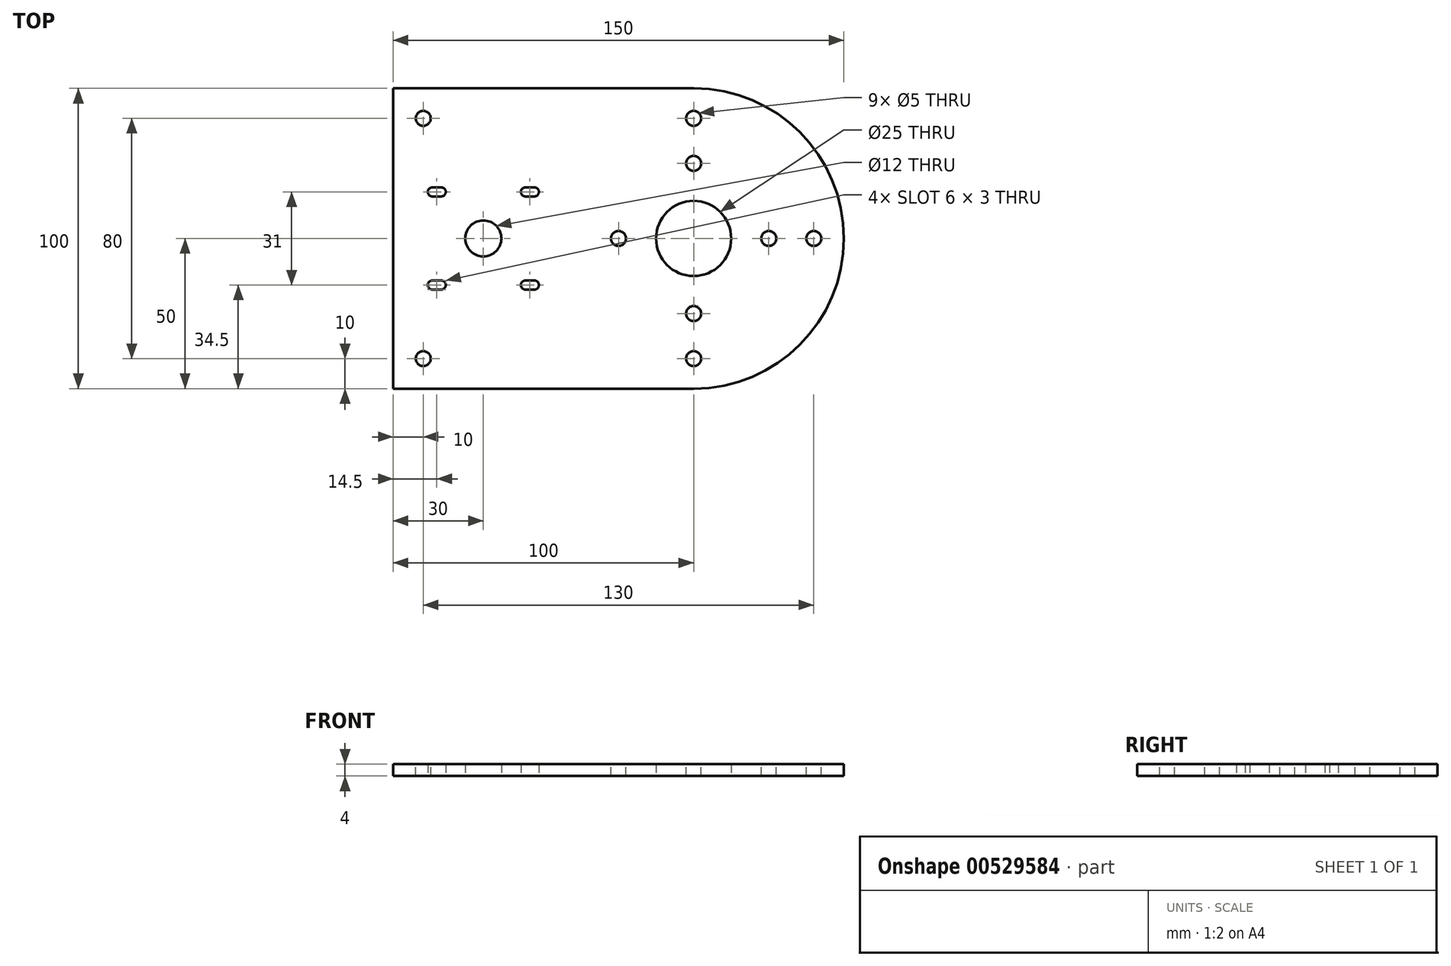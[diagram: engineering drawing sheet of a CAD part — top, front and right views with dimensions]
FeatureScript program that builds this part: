
annotation { "Feature Type Name" : "Feature", "Feature Type Description" : "" }
export const myFeature = defineFeature(function(context is Context, id is Id, definition is map)
    precondition{}
    {
        {
            var Q0;
            Q0=qCreatedBy(makeId("Top.planeOp"),FACE);
            var sketch = newSketch(context, id + "F0", { "sketchPlane" : qUnion([Q0])});
            skArc(sketch, "E0", {"start": v(0, -50) * mm, "mid": v(50, 0) * mm, "end": v(0, 50) * mm});
            skLineSegment(sketch, "E1", {"start": v(0, 50) * mm, "end": v(-100, 50) * mm});
            skLineSegment(sketch, "E2", {"start": v(-100, 50) * mm, "end": v(-100, -50) * mm});
            skLineSegment(sketch, "E3", {"start": v(-100, -50) * mm, "end": v(0, -50) * mm});
            skCircle(sketch, "E4", {"center": v(0, 0) * mm, "radius": 12.5 * mm});
            skPoint(sketch, "E5", {"position": v(-70, 0) * mm});
            skCircle(sketch, "E6", {"center": v(-70, 0) * mm, "radius": 6 * mm});
            skLineSegment(sketch, "E7.bottom", {"start": v(-53, -14) * mm, "end": v(-56, -14) * mm});
            skLineSegment(sketch, "E7.top", {"start": v(-53, -17) * mm, "end": v(-56, -17) * mm});
            skLineSegment(sketch, "E7.left", {"start": v(-53, -14) * mm, "end": v(-53, -17) * mm, "construction": true});
            skLineSegment(sketch, "E7.right", {"start": v(-56, -14) * mm, "end": v(-56, -17) * mm, "construction": true});
            skPoint(sketch, "E7.middle", {"position": v(-54.5, -15.5) * mm});
            skArc(sketch, "E8", {"start": v(-53, -17) * mm, "mid": v(-51.5, -15.5) * mm, "end": v(-53, -14) * mm});
            skArc(sketch, "E9", {"start": v(-56, -14) * mm, "mid": v(-57.5, -15.5) * mm, "end": v(-56, -17) * mm});
            skArc(sketch, "E10.0.1.0", {"start": v(-56, 17) * mm, "mid": v(-57.5, 15.5) * mm, "end": v(-56, 14) * mm});
            skLineSegment(sketch, "E10.0.1.1", {"start": v(-53, 17) * mm, "end": v(-56, 17) * mm});
            skArc(sketch, "E10.0.1.2", {"start": v(-53, 14) * mm, "mid": v(-51.5, 15.5) * mm, "end": v(-53, 17) * mm});
            skLineSegment(sketch, "E10.0.1.3", {"start": v(-53, 14) * mm, "end": v(-56, 14) * mm});
            skArc(sketch, "E10.1.0.0", {"start": v(-87, -14) * mm, "mid": v(-88.5, -15.5) * mm, "end": v(-87, -17) * mm});
            skLineSegment(sketch, "E10.1.0.1", {"start": v(-84, -14) * mm, "end": v(-87, -14) * mm});
            skArc(sketch, "E10.1.0.2", {"start": v(-84, -17) * mm, "mid": v(-82.5, -15.5) * mm, "end": v(-84, -14) * mm});
            skLineSegment(sketch, "E10.1.0.3", {"start": v(-84, -17) * mm, "end": v(-87, -17) * mm});
            skArc(sketch, "E10.1.1.0", {"start": v(-87, 17) * mm, "mid": v(-88.5, 15.5) * mm, "end": v(-87, 14) * mm});
            skLineSegment(sketch, "E10.1.1.1", {"start": v(-84, 17) * mm, "end": v(-87, 17) * mm});
            skArc(sketch, "E10.1.1.2", {"start": v(-84, 14) * mm, "mid": v(-82.5, 15.5) * mm, "end": v(-84, 17) * mm});
            skLineSegment(sketch, "E10.1.1.3", {"start": v(-84, 14) * mm, "end": v(-87, 14) * mm});
            skLineSegment(sketch, "E10.direction1", {"start": v(-56, -17) * mm, "end": v(-87, -17) * mm, "construction": true});
            skLineSegment(sketch, "E10.direction2", {"start": v(-56, -17) * mm, "end": v(-56, 14) * mm, "construction": true});
            skSolve(sketch);
        }
        {
            var Q0;
            Q0=makeQuery(id+"F0.imprint","IMPRINT",FACE,{"disambiguationData":[TD([[makeQuery(id+"F0.imprint","IMPRINT",EDGE,{"derivedFrom":sQuery(id+"F0.wireOp",EDGE,"E0")}),1.0]])]});
            extrude(context, id + "F1", {"entities" : qUnion([Q0]), "depth" : 4 * mm, "offsetDistance" : 25 * mm});
        }
        {
            var Q0;
            Q0=makeQuery(id+"F1.opExtrude","CAP_FACE",FACE,{"disambiguationData":[OSD([sQuery(id+"F0.wireOp",EDGE,"E0"),sQuery(id+"F0.wireOp",EDGE,"E1"),sQuery(id+"F0.wireOp",EDGE,"E2"),sQuery(id+"F0.wireOp",EDGE,"E3"),sQuery(id+"F0.wireOp",EDGE,"E4"),sQuery(id+"F0.wireOp",EDGE,"E6"),sQuery(id+"F0.wireOp",EDGE,"E7.bottom"),sQuery(id+"F0.wireOp",EDGE,"E7.top"),sQuery(id+"F0.wireOp",EDGE,"E8"),sQuery(id+"F0.wireOp",EDGE,"E9"),sQuery(id+"F0.wireOp",EDGE,"E10.0.1.0"),sQuery(id+"F0.wireOp",EDGE,"E10.0.1.1"),sQuery(id+"F0.wireOp",EDGE,"E10.0.1.2"),sQuery(id+"F0.wireOp",EDGE,"E10.0.1.3"),sQuery(id+"F0.wireOp",EDGE,"E10.1.0.0"),sQuery(id+"F0.wireOp",EDGE,"E10.1.0.1"),sQuery(id+"F0.wireOp",EDGE,"E10.1.0.2"),sQuery(id+"F0.wireOp",EDGE,"E10.1.0.3"),sQuery(id+"F0.wireOp",EDGE,"E10.1.1.0"),sQuery(id+"F0.wireOp",EDGE,"E10.1.1.1"),sQuery(id+"F0.wireOp",EDGE,"E10.1.1.2"),sQuery(id+"F0.wireOp",EDGE,"E10.1.1.3")])],"isStart":false});
            var sketch = newSketch(context, id + "F2", { "sketchPlane" : qUnion([Q0])});
            skPoint(sketch, "E11", {"position": v(0, 40) * mm});
            skPoint(sketch, "E12", {"position": v(40, 0) * mm});
            skPoint(sketch, "E13", {"position": v(0, -40) * mm});
            skPoint(sketch, "E14", {"position": v(-90, 40) * mm});
            skPoint(sketch, "E15", {"position": v(-90, -40) * mm});
            skPoint(sketch, "E16", {"position": v(0, 25) * mm});
            skPoint(sketch, "E17.1.0", {"position": v(-25, 0) * mm});
            skPoint(sketch, "E17.2.0", {"position": v(0, -25) * mm});
            skPoint(sketch, "E17.3.0", {"position": v(25, 0) * mm});
            skPoint(sketch, "E17.center", {"position": v(0, 0) * mm});
            skSolve(sketch);
        }
        {
            var Q0;
            Q0=sQuery(id+"F2.wireOp",VERTEX,"E11");
            var Q1;
            Q1=sQuery(id+"F2.wireOp",VERTEX,"E12");
            var Q2;
            Q2=sQuery(id+"F2.wireOp",VERTEX,"E13");
            var Q3;
            Q3=sQuery(id+"F2.wireOp",VERTEX,"E14");
            var Q4;
            Q4=sQuery(id+"F2.wireOp",VERTEX,"E15");
            var Q5;
            Q5=sQuery(id+"F2.wireOp",VERTEX,"E16");
            var Q6;
            Q6=sQuery(id+"F2.wireOp",VERTEX,"E17.3.0");
            var Q7;
            Q7=sQuery(id+"F2.wireOp",VERTEX,"E17.2.0");
            var Q8;
            Q8=sQuery(id+"F2.wireOp",VERTEX,"E17.1.0");
            var Q9;
            Q9=makeQuery(id+"F1.opExtrude","SWEPT_BODY",BODY,{"disambiguationData":[OSD([sQuery(id+"F0.wireOp",EDGE,"E0"),sQuery(id+"F0.wireOp",EDGE,"E1"),sQuery(id+"F0.wireOp",EDGE,"E2"),sQuery(id+"F0.wireOp",EDGE,"E3"),sQuery(id+"F0.wireOp",EDGE,"E4"),sQuery(id+"F0.wireOp",EDGE,"E6"),sQuery(id+"F0.wireOp",EDGE,"E7.bottom"),sQuery(id+"F0.wireOp",EDGE,"E7.top"),sQuery(id+"F0.wireOp",EDGE,"E8"),sQuery(id+"F0.wireOp",EDGE,"E9"),sQuery(id+"F0.wireOp",EDGE,"E10.0.1.0"),sQuery(id+"F0.wireOp",EDGE,"E10.0.1.1"),sQuery(id+"F0.wireOp",EDGE,"E10.0.1.2"),sQuery(id+"F0.wireOp",EDGE,"E10.0.1.3"),sQuery(id+"F0.wireOp",EDGE,"E10.1.0.0"),sQuery(id+"F0.wireOp",EDGE,"E10.1.0.1"),sQuery(id+"F0.wireOp",EDGE,"E10.1.0.2"),sQuery(id+"F0.wireOp",EDGE,"E10.1.0.3"),sQuery(id+"F0.wireOp",EDGE,"E10.1.1.0"),sQuery(id+"F0.wireOp",EDGE,"E10.1.1.1"),sQuery(id+"F0.wireOp",EDGE,"E10.1.1.2"),sQuery(id+"F0.wireOp",EDGE,"E10.1.1.3")])]});
            hole(context, id + "F3", {"style" : HoleStyle.SIMPLE, "endStyle" : HoleEndStyle.THROUGH, "standardTappedOrClearance" : lookupTablePath({ "standard" : "ISO", "engagement" : "75%", "pitch" : "1 mm", "size" : "M6", "type" : "Tapped" }), "standardBlindInLast" : lookupTablePath({ "standard" : "ISO", "engagement" : "75%", "pitch" : "1 mm", "size" : "M6", "type" : "Tapped" }), "holeDiameter" : 5 * mm, "showTappedDepth" : true, "isTappedThrough" : true, "tappedDepth" : 9 * mm, "tapClearance" : 3, "locations" : qUnion([Q0, Q1, Q2, Q3, Q4, Q5, Q6, Q7, Q8]), "scope" : qUnion([Q9]), "majorDiameter" : 6 * mm});
        }
    });
